# Revit family: NBS_Allermuir_OffcChrs_Kin_HighBackStool
name_source: partatom
category: Furniture
revit_build: Autodesk Revit 2018 (Build: 20190510_1515(x64)
units: mm (PartAtom-declared; Revit-internal decimal feet)

## family parameters
Always vertical = Yes
Cut with Voids When Loaded = No
Room Calculation Point = No
Shared = No
Work Plane-Based = No

## types (1)
- Kin_HighBackStool_KIN602
    AssetType = Movable
    BIMObjectName = NBS_Allermuir_OfficeChairs_Kin_HighBackStool_KIN602
    Category = Pr_40_50_12_57:Office chairs
    CodePerformance = ANSI/BIFMA X5.1-2017
    Color = Off-Black, White, Crayon Grey, Pistachio, Haze Blue, Aubergine, Seattle Green, Red
    Description = High back stool on 4 leg frame
    DurationUnit = year
    ExpectedLife = 10
    Features = Plastic shell — Colour: Off-Black, Tubular steel frame finished in Off-Black powder coat, Footrest protector, Plastic glides, Counter height option available, Plastic glides with felt
    Finish = Off-Black, White, Crayon Grey, Pistachio, Haze Blue, Aubergine, Seattle Green, Red
    FrameFinish = Off-Black, White, Crayon Grey, Pistachio, Haze Blue, Aubergine, Seattle Green, Red
    FrameMaterial = NBS_Allermuir_Steel_BlackPowderCoat
    HighestSeatingHeight = 0 mm  [stored 0 ft]
    IfcExportAs = IfcFurnitureType
    IfcExportType = STOOL
    IsBuiltIn = No
    LowestSeatingHeight = 0 mm  [stored 0 ft]
    ManufacturerName = Allermuir
    ManufacturerURL = www.allermuir.co.uk
    Material = Polypropylene, Aluminium Casting
    ModelNumber = KIN602
    ModelReference = Kin_HighBackStool
    NBSCertification = www.nationalbimlibrary.com/cert/mq5gtigc
    NBSDescription = Office chairs
    NBSReference = 45-35-20/330
    Name = OfficeChairs_KIN602_Kin_Allermuir
    NominalDepth = 535 mm  [stored 1.75525 ft]
    NominalHeight = 1115 mm
    NominalLength = 460 mm  [stored 1.50919 ft]
    NominalWidth = 460 mm  [stored 1.50919 ft]
    PlasticAndMetalFinish = Off-Black, White, Crayon Grey, Pistachio, Haze Blue, Aubergine, Seattle Green, Red
    ProductInformation = https://www.allermuir.com
    SeatDepth = 535 mm
    SeatMaterial = NBS_Allermuir_Plastic_Black
    SeatWidth = 460 mm
    SeatingHeight = 745 mm  [stored 2.44423 ft]
    Size = 535 x 1115 x 745 mm
    Status = UNSET
    Style = Stool
    SustainabilityPerformance = 99% recyclable
    Uniclass2015Code = Pr_40_50_12_57
    Uniclass2015Title = Office chairs
    Uniclass2015Version = Products v1.15
    Version = 1
    WarrantyDescription = Allermuir warrant that its manufactured products are free from manufacturing defects - in materials or workmanship - for a period of five (5) years. , Allermuir will repair, or replace (at Allermuir's sole discretion) with comparable free of charge materials / components, any product / component which fails under normal use in a single shift environment, as a result of a defect in the materials and/ or workmanship
    WarrantyDurationParts = 5
    WarrantyDurationUnit = year

note: [stored X ft] marks values corroborated as IEEE doubles in the binary element streams (Revit-internal decimal feet)

## geometry (parser evidence)
native form markers: Sweep x3
no freeform markers — native parametric forms only
